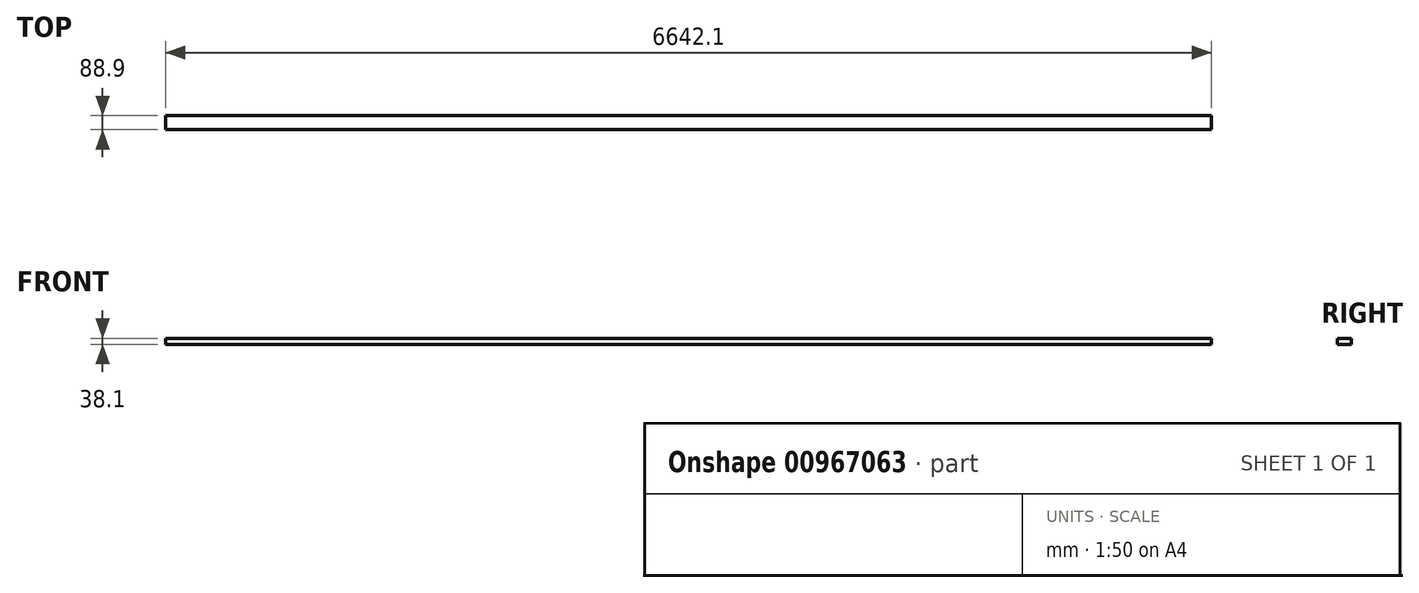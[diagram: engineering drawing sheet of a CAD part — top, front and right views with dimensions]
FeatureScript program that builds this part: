
annotation { "Feature Type Name" : "Feature", "Feature Type Description" : "" }
export const myFeature = defineFeature(function(context is Context, id is Id, definition is map)
    precondition{}
    {
        {
            var Q0;
            Q0=qCreatedBy(makeId("Right.planeOp"),FACE);
            var sketch = newSketch(context, id + "F0", { "sketchPlane" : qUnion([Q0])});
            skLineSegment(sketch, "E0.bottom", {"start": v(0, 0) * mm, "end": v(88.9, 0) * mm});
            skLineSegment(sketch, "E0.top", {"start": v(0, 38.1) * mm, "end": v(88.9, 38.1) * mm});
            skLineSegment(sketch, "E0.left", {"start": v(0, 0) * mm, "end": v(0, 38.1) * mm});
            skLineSegment(sketch, "E0.right", {"start": v(88.9, 0) * mm, "end": v(88.9, 38.1) * mm});
            skSolve(sketch);
        }
        {
            var Q0;
            Q0 = qSketchRegion(id + "F0", true);
            extrude(context, id + "F1", {"entities" : qUnion([Q0]), "oppositeDirection" : true, "depth" : 6642.1 * mm, "offsetDistance" : 25.4 * mm});
        }
    });
